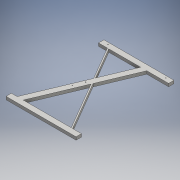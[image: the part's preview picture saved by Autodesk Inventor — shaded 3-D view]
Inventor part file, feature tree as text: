
AUTODESK INVENTOR PART (.ipt)
format: ipt  version: 2016 (Build 200138000, 138)  size: 144,896 bytes
history: native  units: mm
features: extrude x2, thread x2, sketch x2
ambient origin geometry x8: Origin, YZ Plane, XZ Plane, XY Plane, X Axis, Y Axis, Z Axis, Center Point
bodies: 实体1 (feature_tree)
feature tree (6):
  extrude  "拉伸1"  Depth=40.0mm
  extrude  "拉伸2"  Depth=10.0mm
  thread  "螺纹1"  [1 undecoded]
  thread  "螺纹2"  [1 undecoded]
  sketch  "草图1"  dims[d0=520.0mm d1=40.0mm]
  sketch  "草图2"  dims[d2=162.0mm d3=45.0mm d4=647.0mm d5=40.0mm d6=43.0mm d7=66.0mm d8=66.0mm d9=10.0mm d10=22.0mm d11=0.0mm d12=45.0mm d13=5.0mm d14=15.0mm d15=45.0mm d16=15.0mm d17=5.0mm d23=25.0mm d24=0.0mm d46=5.0mm d47=5.0mm d48=75.0mm d49=10.0mm d50=0.0mm d51=10.0mm d52=0.0mm]
note: 2 required parameter values undecoded (feature->parameter linkage not recoverable at this tier; creation-order binding heuristic only, values carry confidence <= 0.55)
